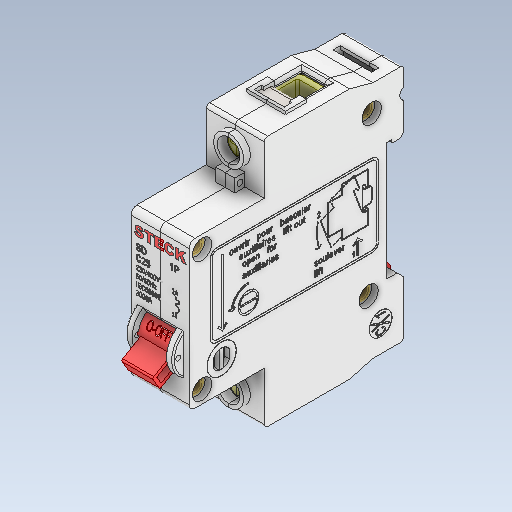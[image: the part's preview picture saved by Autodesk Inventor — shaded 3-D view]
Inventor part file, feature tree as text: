
AUTODESK INVENTOR PART (.ipt)
format: ipt  version: 2025.2 (Build 292293000, 293)  size: 5,760,000 bytes
history: native  units: mm
features: other x46, sketch x4
ambient origin geometry x8: Origin, YZ Plane, XZ Plane, XY Plane, X Axis, Y Axis, Z Axis, Center Point
bodies: Body1 (feature_tree), Body2 (feature_tree), Body3 (feature_tree), Body4 (feature_tree), Body5 (feature_tree), Body6 (feature_tree), Body7 (feature_tree), Body8 (feature_tree), Body9 (feature_tree), Body10 (feature_tree), Body11 (feature_tree), Body12 (feature_tree), Body13 (feature_tree), Body14 (feature_tree), Body15 (feature_tree), Body16 (feature_tree), Body17 (feature_tree), Body18 (feature_tree), Body19 (feature_tree), Body20 (feature_tree), Body21 (feature_tree), Body22 (feature_tree), Body23 (feature_tree), Body24 (feature_tree), Body25 (feature_tree)
feature tree (50):
  other  "Sólido1"
  other  "Sólido2"
  other  "Sólido3"
  other  "Sólido4"
  other  "Sólido5"
  other  "Sólido6"
  other  "Sólido7"
  other  "Sólido8"
  other  "Sólido9"
  other  "Sólido10"
  other  "Sólido11"
  other  "Sólido12"
  other  "Sólido13"
  other  "Sólido14"
  other  "Sólido15"
  other  "Sólido16"
  other  "Sólido17"
  other  "Sólido18"
  other  "Sólido19"
  other  "Sólido20"
  other  "Sólido21"
  other  "Sólido22"
  other  "Sólido23"
  other  "Sólido24"
  other  "Sólido25"
  other  "Chanfro4"
  other  "Inclinação3"
  other  "Espelhar1[1]"
  other  "Espelhar1[2]"
  other  "Envolver1"
  other  "Filete11"
  other  "Revolução1"
  sketch  "Esboço-padrão1[1]"
  sketch  "Esboço-padrão1[2]"
  sketch  "Esboço-padrão1[3]"
  sketch  "Esboço-padrão1[4]"
  other  "Ressalto-extrusão38"
  other  "Ressalto-extrusão31[2]"
  other  "Ressalto-extrusão31[3]"
  other  "Ressalto-extrusão37[2]"
  other  "Ressalto-extrusão37[3]"
  other  "Ressalto-extrusão37[4]"
  other  "Ressalto-extrusão37[5]"
  other  "Dividir1[1]"
  other  "Dividir1[2]"
  other  "Dividir1[3]"
  other  "Dividir1[4]"
  other  "Dividir1[5]"
  other  "Dividir1[6]"
  other  "Dividir1[7]"
